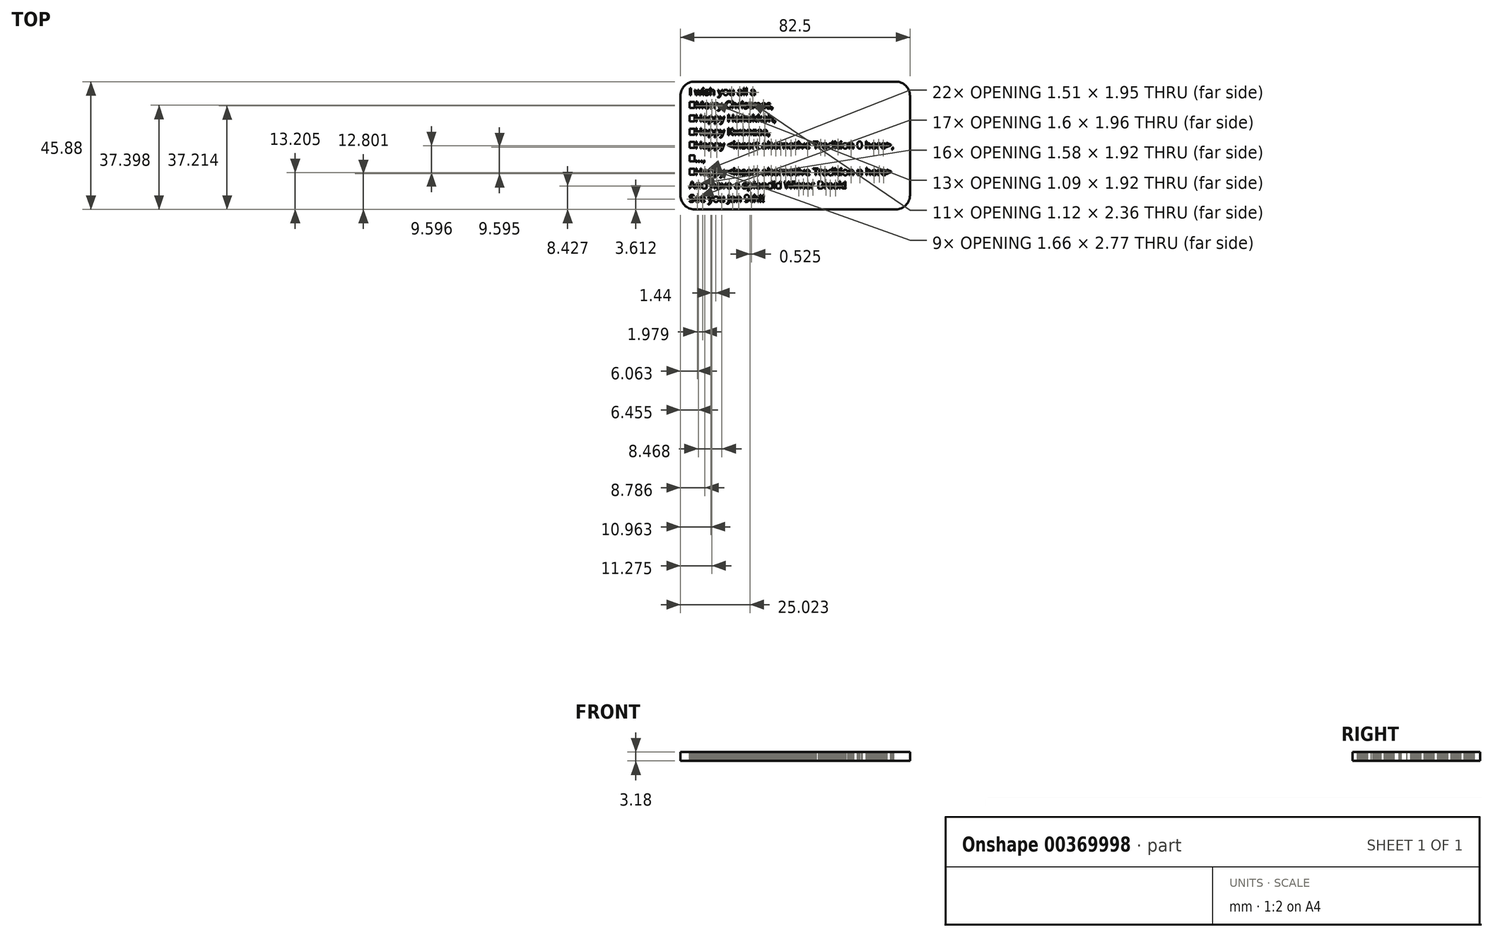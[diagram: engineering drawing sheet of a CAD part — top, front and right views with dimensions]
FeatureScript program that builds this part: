
annotation { "Feature Type Name" : "Feature", "Feature Type Description" : "" }
export const myFeature = defineFeature(function(context is Context, id is Id, definition is map)
    precondition{}
    {
        {
            var Q0;
            Q0=qCreatedBy(makeId("Top.planeOp"),FACE);
            var sketch = newSketch(context, id + "F0", { "sketchPlane" : qUnion([Q0])});
            skPoint(sketch, "E0.middle", {"position": v(0, 0) * mm});
            skText(sketch, "E1", { "text": "I wish you all a \n	Merry Christmas,\n	Happy Hanukkah,\n	Happy Kwanzaa,\n	Happy <insert alternative Tradition 0 here>,\n	...,\n	Happy <insert alternative Tradition n here>\nAnd have a splendid Winter Break!\nSee you Jan 9th!!", "fontName": "OpenSans-Regular.ttf"});
            skLineSegment(sketch, "E2.bottom", {"start": v(-5.14, 3.53) * mm, "end": v(77.36, 3.53) * mm});
            skLineSegment(sketch, "E2.top", {"start": v(-5.14, -42.35) * mm, "end": v(77.36, -42.35) * mm});
            skLineSegment(sketch, "E2.left", {"start": v(-5.14, 3.53) * mm, "end": v(-5.14, -42.35) * mm});
            skLineSegment(sketch, "E2.right", {"start": v(77.36, 3.53) * mm, "end": v(77.36, -42.35) * mm});
            const initialGuessF0  = {"E1": [-0.00201, -0.0013, 1, 0, 0.00254]};
            skSetInitialGuess(sketch, initialGuessF0);
            skSolve(sketch);
        }
        {
            var Q0;
            Q0=makeQuery(id+"F0.imprint","IMPRINT",FACE,{"disambiguationData":[TD([[makeQuery(id+"F0.imprint","IMPRINT",EDGE,{"derivedFrom":sQuery(id+"F0.wireOp",EDGE,"E1.sketch_text.stroke-0")}),1.0]])]});
            extrude(context, id + "F1", {"entities" : qUnion([Q0]), "depth" : 3.17 * mm});
        }
        {
            var Q0;
            Q0=makeQuery(id+"F1.opExtrude","SWEPT_EDGE",EDGE,{"disambiguationData":[OSD([sQuery(id+"F0.wireOp",EDGE,"E2.bottom"),sQuery(id+"F0.wireOp",EDGE,"E2.left")])]});
            var Q1;
            Q1=makeQuery(id+"F1.opExtrude","SWEPT_EDGE",EDGE,{"disambiguationData":[OSD([sQuery(id+"F0.wireOp",EDGE,"E2.bottom"),sQuery(id+"F0.wireOp",EDGE,"E2.right")])]});
            var Q2;
            Q2=makeQuery(id+"F1.opExtrude","SWEPT_EDGE",EDGE,{"disambiguationData":[OSD([sQuery(id+"F0.wireOp",EDGE,"E2.top"),sQuery(id+"F0.wireOp",EDGE,"E2.right")])]});
            var Q3;
            Q3=makeQuery(id+"F1.opExtrude","SWEPT_EDGE",EDGE,{"disambiguationData":[OSD([sQuery(id+"F0.wireOp",EDGE,"E2.top"),sQuery(id+"F0.wireOp",EDGE,"E2.left")])]});
            fillet(context, id + "F2", {"entities" : qUnion([Q0, Q1, Q2, Q3]), "radius" : 5.08 * mm, "tangentPropagation" : true, "allowEdgeOverflow" : false});
        }
    });
